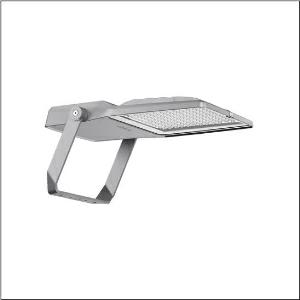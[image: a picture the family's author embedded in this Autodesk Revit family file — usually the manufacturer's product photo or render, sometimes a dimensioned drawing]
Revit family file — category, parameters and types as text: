
# Revit family: floodlight_fl_21_iq_midi___rs12_5xa7782e4b1a_b2fd
name_source: partatom
category: Lighting Fixtures
units: mm (PartAtom-declared; Revit-internal decimal feet)

## family parameters
Cut with Voids When Loaded = No
Host = Face
Light Source = No
Part Type = Normal
Room Calculation Point = No
Round Connector Dimension = Use Diameter
Shared = No

## types (1)
- --- (1 x LED, 27880 lm, 208.1 W, 4000K)
    Apparent Load = 208 VA
    CIE Flux Codes = 79 92 99 100 100
    Color Rendering = 70
    Color Temperature = 4000K
    Default Elevation = 1800 mm
    Description = Floodlight FL 21 iQ midi, floodlight, primary light control with lens, of PMMA, primary optical cover: protective disc, of toughened safety glass, transparent, light distribution: RS12, light emission: direct distribution, installation type: surface-mounted, LED, High Power LED, rated luminous flux: 27.880lm, luminous efficacy: 134lm/W, light colour: 740, colour temperature: 4000K, control gear: ECG iQ, control: optimised constant luminous flux control (CLO 2.0), Desk-Remote (wireless, voltage-free reading and setting of iQ features in the workshop via application-optimized NFC function/RFID function), Smart-Wire, Night-Set, Temp-Guard, Street-Remote, Auto-Match, with terminal, 6-pole, mains connection: 220..240V, AC, 50/60Hz, start of lifetime: 208W, end of service life: 227W, reduction: 90W, luminaire housing, of diecast aluminium, powder-coated, Siteco® metallic grey (DB 702S), corrosivity category C5 mid according to DIN EN ISO 12944, sealing non-destructively replaceable, mounting bracket, of steel, galvanised, powder-coated, Siteco® metallic grey (DB 702S), protection rating (complete): IP66, insulation class (complete): insulation class II (safety insulation), certification: CE, protection symbol: D, impact resistance: IK08, permissible operating ambient temperature: -40..+40°C, permissible operating ambient temperature for outdoor applications: -40..+50°C, standard: DIN EN 12944, LABS conformity tested according to VDMA 24364:2018-05, packaging unit: 1 piece

Light Distribution: RS12
    Height = 76 mm
    Lamp = 1 x LED
    Lamp Light Flux = 27880 lm
    Lamp Power = 208.1 W
    Lamp count = 1
    Length = 657 mm
    Luminous efficacy = 134 lm/W
    Manufacturer = Siteco
    ModVariant = No
    Model = 5XA7782E4B1A
    Number of Poles = 1
    OnlyDefault = Yes
    Power Factor = 1
    Product Name = Floodlight FL 21 iQ midi | RS12
    Product group = floodlight | pylon annexe
    ProductGroupID = 6200
    Protection Class = Protection class II
    Protection Degree = IP 66
    RLX_Detail_Level = 1
    RLX_Emergency_Light_Flux = 0 lm
    RLX_Emergency_Type = 0
    RLX_Emergency_Type_DB = No
    RlxData = <blob elided: 141301 chars, md5=d094f80c>
    Socket = socket
    Standby Power = 0 W
    System Light Flux = 27880 lm
    System Power = 208 W
    Type Comments = factory setting: luminous flux: 100 % | dim-lin: 254 | 710 mA
    Type Image = l_1006876.jpg
    URL = http://relux.com
    VarID = @adj_037869
    Voltage = 0 V
    Weight = 0.00 kg
    Width = 442 mm

## geometry (parser evidence)
native form markers: Blend x4, Sweep x12
no freeform markers — native parametric forms only
